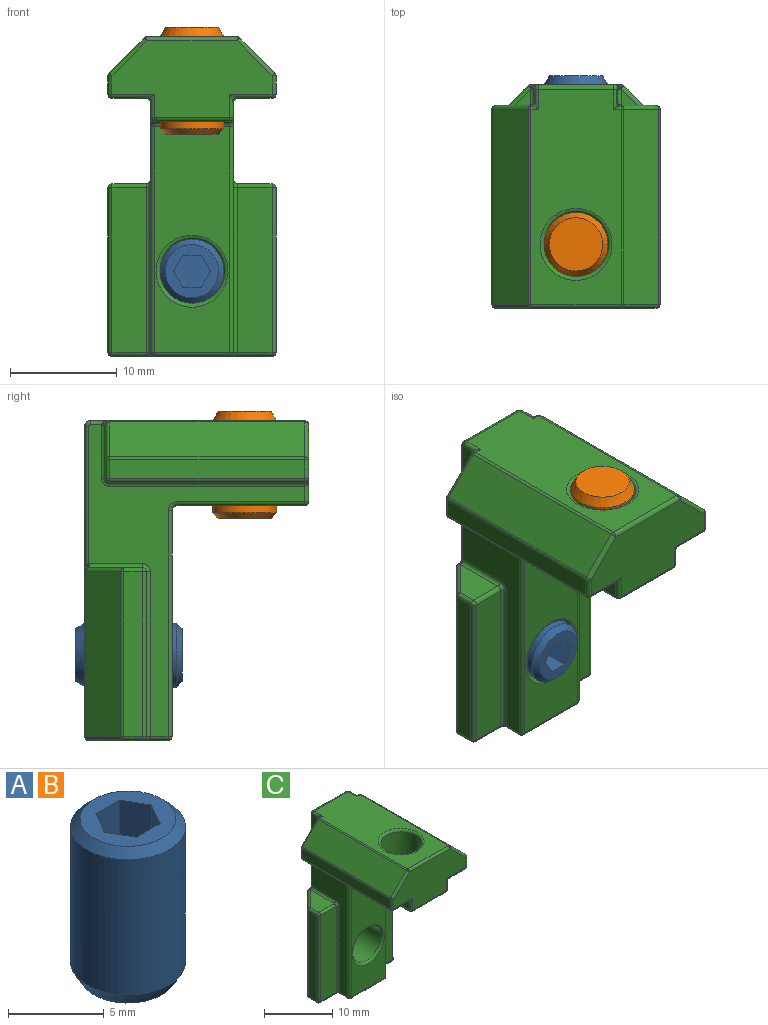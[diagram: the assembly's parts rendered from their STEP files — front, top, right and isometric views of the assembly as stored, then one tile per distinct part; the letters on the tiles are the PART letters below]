
ASSEMBLY  parts=3 mates=2
PART A: 12 faces, bbox 6x6x10 mm
  f0: cone r=3mm half-angle=45deg, axis (0,0,-1), area 12.2mm2, adj f2,f3
  f1: cone r=2.5mm half-angle=30deg, axis (0,0,1), area 17.3mm2, adj f2,f4
  f2: cylinder r=3mm len=8.63mm, axis (0,0,-1), area 162.7mm2, adj f0,f1
  f3: plane 5x5mm, normal (0,0,1), area 11.8mm2, adj f0,f5,f6,f7,f8,f9,f10
  f4: plane 5x5mm, normal (0,0,-1), area 19.6mm2, adj f1
  f5: plane 3x1.73mm, normal (0,-1,0), area 5.2mm2, adj f3,f6,f10,f11
  f6: plane 3x1.5mm, normal (-0.87,-0.5,0), area 5.2mm2, adj f3,f5,f7,f11
  f7: plane 3x1.5mm, normal (-0.87,0.5,0), area 5.2mm2, adj f3,f6,f8,f11
  f8: plane 3x1.73mm, normal (0,1,0), area 5.2mm2, adj f3,f7,f9,f11
  f9: plane 3x1.5mm, normal (0.87,0.5,0), area 5.2mm2, adj f3,f8,f10,f11
  f10: plane 3x1.5mm, normal (0.87,-0.5,0), area 5.2mm2, adj f3,f5,f9,f11
  f11: plane 3.46x3mm, normal (0,0,1), area 7.8mm2, adj f5,f6,f7,f8,f9,f10
PART B: same geometry as A
PART C: 152 faces, bbox 15.8x21x30 mm
  f0: torus R=3.38mm, axis (0,1,0), area 11.8mm2, adj f5,f10
  f1: torus R=3.38mm, axis (0,-1,0), area 11.8mm2, adj f5,f6
  f2: torus R=3.38mm, axis (0,0,1), area 11.8mm2, adj f4,f9
  f3: torus R=3.38mm, axis (0,0,-1), area 11.8mm2, adj f4,f7
  f4: cylinder r=3mm len=7.19mm, axis (0,0,-1), area 135.5mm2, adj f2,f3
  f5: cylinder r=3mm len=7.44mm, axis (0,-1,0), area 140.3mm2, adj f0,f1
  f6: plane 29.11x8.45mm, normal (0,1,0), area 190.7mm2, adj f1,f31,f32,f33,f34,f37,f40,f41
  f7: plane 20.12x8.45mm, normal (0,0,1), area 131.4mm2, adj f3,f31,f45,f50,f51,f60,f67,f74
  f8: plane 15.01x7.19mm, normal (0,-1,0), area 79.9mm2, adj f75,f82,f91,f99,f104,f109,f112,f113
  f9: plane 11.91x7.04mm, normal (0,0,-1), area 47.9mm2, adj f2,f30,f114,f115,f119
  f10: plane 21.16x7.04mm, normal (0,-1,0), area 113mm2, adj f0,f30,f95,f106,f107
  f11: plane 15.01x7.44mm, normal (0,0,-1), area 81.7mm2, adj f41,f55,f56,f70,f71,f86,f87,f94
  f12: plane 29.24x20.24mm, normal (1,0,0), area 105.8mm2, adj f34,f38,f45,f94,f106,f110,f113,f114
  f13: plane 29.24x20.25mm, normal (-1,0,0), area 105.8mm2, adj f37,f44,f50,f96,f107,f111,f115,f116
  f14: plane 15.44x3.28mm, normal (-0.71,0.71,0), area 71.7mm2, adj f42,f43,f56,f57
  f15: plane 15.44x1.75mm, normal (-1,0,0), area 27mm2, adj f57,f58,f71,f72
  f16: plane 4.97x3.23mm, normal (0,0,1), area 10.8mm2, adj f43,f58,f59,f141
  f17: plane 15.44x3.23mm, normal (0,-1,0), area 49.8mm2, adj f59,f72,f87,f142
  f18: plane 15.44x3.23mm, normal (0,-1,0), area 49.8mm2, adj f52,f69,f86,f149
  f19: plane 4.97x3.23mm, normal (0,0,1), area 10.8mm2, adj f39,f52,f53,f150
  f20: plane 15.44x1.75mm, normal (1,0,0), area 27mm2, adj f53,f54,f69,f70
  f21: plane 15.44x3.28mm, normal (0.71,0.71,0), area 71.7mm2, adj f39,f40,f54,f55
  f22: plane 18.29x1.75mm, normal (-1,0,0), area 32mm2, adj f89,f90,f103,f104
  f23: plane 18.29x3.28mm, normal (-0.71,0,0.71), area 84.9mm2, adj f73,f74,f90,f91
  f24: plane 4.97x3.23mm, normal (0,1,0), area 10.8mm2, adj f73,f88,f89,f123
  f25: plane 18.29x3.23mm, normal (0,0,-1), area 59mm2, adj f88,f103,f112,f121
  f26: plane 18.29x3.23mm, normal (0,0,-1), area 59mm2, adj f85,f100,f109,f129
  f27: plane 4.97x3.23mm, normal (0,1,0), area 10.8mm2, adj f68,f84,f85,f131
  f28: plane 18.29x3.28mm, normal (0.71,0,0.71), area 84.9mm2, adj f67,f68,f82,f83
  f29: plane 18.29x1.75mm, normal (1,0,0), area 32mm2, adj f83,f84,f99,f100
  f30: cylinder r=0.51mm len=7.04mm, axis (1,0,0), area 5.6mm2, adj f9,f10,f110,f111
  f31: cylinder r=0.51mm len=7.04mm, axis (-1,0,0), area 5.6mm2, adj f6,f7,f38,f44
  f32: cylinder r=0.38mm len=0.71mm, axis (1,0,0), area 0.2mm2, adj f6,f35,f144
  f33: cylinder r=0.38mm len=0.71mm, axis (1,0,0), area 0.2mm2, adj f6,f36,f136
  f34: cylinder r=0.38mm len=13.67mm, axis (0,0,1), area 7.9mm2, adj f6,f12,f38,f144,f145,f146
  f35: sphere r=0.38mm, area 0.1mm2, adj f32,f39,f40,f145
  f36: sphere r=0.38mm, area 0.1mm2, adj f33,f42,f43,f137
  f37: cylinder r=0.38mm len=13.67mm, axis (0,0,-1), area 7.9mm2, adj f6,f13,f44,f136,f137,f138
  f38: torus R=0.13mm, axis (-1,0,0), area 0.3mm2, adj f12,f31,f34,f45
  f39: cylinder r=0.38mm len=3.55mm, axis (-0.71,0.71,0), area 2.8mm2, adj f19,f21,f35,f46,f146,f148
  f40: cylinder r=0.38mm len=15.44mm, axis (0,0,1), area 4.6mm2, adj f6,f21,f35,f47
  f41: cylinder r=0.38mm len=8.45mm, axis (-1,0,0), area 5.1mm2, adj f6,f11,f47,f48
  f42: cylinder r=0.38mm len=15.44mm, axis (0,0,1), area 4.6mm2, adj f6,f14,f36,f48
  f43: cylinder r=0.38mm len=3.55mm, axis (-0.71,-0.71,0), area 2.8mm2, adj f14,f16,f36,f49,f138,f139
  f44: torus R=0.13mm, axis (-1,0,0), area 0.3mm2, adj f13,f31,f37,f50
  f45: cylinder r=0.38mm len=1.83mm, axis (0,-1,0), area 0.8mm2, adj f7,f12,f38,f133,f134,f135
  f46: sphere r=0.38mm, area 0.1mm2, adj f39,f53,f54
  f47: sphere r=0.38mm, area 0.1mm2, adj f40,f41,f55
  f48: sphere r=0.38mm, area 0.1mm2, adj f41,f42,f56
  f49: sphere r=0.38mm, area 0.1mm2, adj f43,f57,f58
  f50: cylinder r=0.38mm len=1.83mm, axis (0,1,0), area 0.8mm2, adj f7,f13,f44,f125,f126,f127
  f51: cylinder r=0.38mm len=0.71mm, axis (1,0,0), area 0.2mm2, adj f7,f61,f134
  f52: cylinder r=0.38mm len=3.23mm, axis (1,0,0), area 1.9mm2, adj f18,f19,f62,f151
  f53: cylinder r=0.38mm len=1.75mm, axis (0,1,0), area 1mm2, adj f19,f20,f46,f62
  f54: cylinder r=0.38mm len=15.44mm, axis (0,0,-1), area 4.6mm2, adj f20,f21,f46,f63
  f55: cylinder r=0.38mm len=3.55mm, axis (-0.71,0.71,0), area 2.8mm2, adj f11,f21,f47,f63
  f56: cylinder r=0.38mm len=3.55mm, axis (-0.71,-0.71,0), area 2.8mm2, adj f11,f14,f48,f64
  f57: cylinder r=0.38mm len=15.44mm, axis (0,0,-1), area 4.6mm2, adj f14,f15,f49,f64
  f58: cylinder r=0.38mm len=1.75mm, axis (0,-1,0), area 1mm2, adj f15,f16,f49,f65
  f59: cylinder r=0.38mm len=3.23mm, axis (1,0,0), area 1.9mm2, adj f16,f17,f65,f143
  f60: cylinder r=0.38mm len=0.71mm, axis (1,0,0), area 0.2mm2, adj f7,f66,f127
  f61: sphere r=0.38mm, area 0.1mm2, adj f51,f67,f68,f135
  f62: sphere r=0.38mm, area 0.2mm2, adj f52,f53,f69
  f63: sphere r=0.38mm, area 0.1mm2, adj f54,f55,f70
  f64: sphere r=0.38mm, area 0.1mm2, adj f56,f57,f71
  f65: sphere r=0.38mm, area 0.2mm2, adj f58,f59,f72
  f66: sphere r=0.38mm, area 0.1mm2, adj f60,f73,f74,f126
  f67: cylinder r=0.38mm len=18.29mm, axis (0,1,0), area 5.5mm2, adj f7,f28,f61,f76
  f68: cylinder r=0.38mm len=3.55mm, axis (-0.71,0,0.71), area 2.8mm2, adj f27,f28,f61,f77,f132,f133
  f69: cylinder r=0.38mm len=15.44mm, axis (0,0,-1), area 9.2mm2, adj f18,f20,f62,f78
  f70: cylinder r=0.38mm len=1.75mm, axis (0,1,0), area 1mm2, adj f11,f20,f63,f78
  f71: cylinder r=0.38mm len=1.75mm, axis (0,-1,0), area 1mm2, adj f11,f15,f64,f79
  f72: cylinder r=0.38mm len=15.44mm, axis (0,0,-1), area 9.2mm2, adj f15,f17,f65,f79
  f73: cylinder r=0.38mm len=3.55mm, axis (-0.71,0,-0.71), area 2.8mm2, adj f23,f24,f66,f80,f124,f125
  f74: cylinder r=0.38mm len=18.29mm, axis (0,1,0), area 5.5mm2, adj f7,f23,f66,f81
  f75: cylinder r=0.38mm len=8.45mm, axis (-1,0,0), area 5.1mm2, adj f7,f8,f76,f81
  f76: sphere r=0.38mm, area 0.1mm2, adj f67,f75,f82
  f77: sphere r=0.38mm, area 0.1mm2, adj f68,f83,f84
  f78: sphere r=0.38mm, area 0.1mm2, adj f69,f70,f86
  f79: sphere r=0.38mm, area 0.1mm2, adj f71,f72,f87
  f80: sphere r=0.38mm, area 0.1mm2, adj f73,f89,f90
  f81: sphere r=0.38mm, area 0.1mm2, adj f74,f75,f91
  f82: cylinder r=0.38mm len=3.55mm, axis (0.71,0,-0.71), area 2.8mm2, adj f8,f28,f76,f92
  f83: cylinder r=0.38mm len=18.29mm, axis (0,-1,0), area 5.5mm2, adj f28,f29,f77,f92
  f84: cylinder r=0.38mm len=1.75mm, axis (0,0,1), area 1mm2, adj f27,f29,f77,f93
  f85: cylinder r=0.38mm len=3.23mm, axis (1,0,0), area 1.9mm2, adj f26,f27,f93,f130
  f86: cylinder r=0.38mm len=3.99mm, axis (1,0,0), area 2.2mm2, adj f11,f18,f78,f147
  f87: cylinder r=0.38mm len=3.99mm, axis (1,0,0), area 2.2mm2, adj f11,f17,f79,f140
  f88: cylinder r=0.38mm len=3.23mm, axis (1,0,0), area 1.9mm2, adj f24,f25,f97,f122
  f89: cylinder r=0.38mm len=1.75mm, axis (0,0,-1), area 1mm2, adj f22,f24,f80,f97
  f90: cylinder r=0.38mm len=18.29mm, axis (0,-1,0), area 5.5mm2, adj f22,f23,f80,f98
  f91: cylinder r=0.38mm len=3.55mm, axis (0.71,0,0.71), area 2.8mm2, adj f8,f23,f81,f98
  f92: sphere r=0.38mm, area 0.1mm2, adj f82,f83,f99
  f93: sphere r=0.38mm, area 0.1mm2, adj f84,f85,f100
  f94: cylinder r=0.38mm len=2.41mm, axis (0,1,0), area 1.2mm2, adj f11,f12,f101,f147
  f95: cylinder r=0.38mm len=7.04mm, axis (-1,0,0), area 4.2mm2, adj f10,f11,f101,f102
  f96: cylinder r=0.38mm len=2.41mm, axis (0,-1,0), area 1.2mm2, adj f11,f13,f102,f140
  f97: sphere r=0.38mm, area 0.3mm2, adj f88,f89,f103
  f98: sphere r=0.38mm, area 0.1mm2, adj f90,f91,f104
  f99: cylinder r=0.38mm len=1.75mm, axis (0,0,-1), area 1mm2, adj f8,f29,f92,f105
  f100: cylinder r=0.38mm len=18.29mm, axis (0,-1,0), area 10.9mm2, adj f26,f29,f93,f105
  f101: sphere r=0.38mm, area 0.1mm2, adj f94,f95,f106
  f102: sphere r=0.38mm, area 0.3mm2, adj f95,f96,f107
  f103: cylinder r=0.38mm len=18.29mm, axis (0,-1,0), area 10.9mm2, adj f22,f25,f97,f108
  f104: cylinder r=0.38mm len=1.75mm, axis (0,0,1), area 1mm2, adj f8,f22,f98,f108
  f105: sphere r=0.38mm, area 0.1mm2, adj f99,f100,f109
  f106: cylinder r=0.38mm len=21.16mm, axis (0,0,-1), area 12.7mm2, adj f10,f12,f101,f110
  f107: cylinder r=0.38mm len=21.16mm, axis (0,0,1), area 12.7mm2, adj f10,f13,f102,f111
  f108: sphere r=0.38mm, area 0.3mm2, adj f103,f104,f112
  f109: cylinder r=0.38mm len=3.99mm, axis (-1,0,0), area 2.2mm2, adj f8,f26,f105,f128
  f110: torus R=0.89mm, axis (-1,0,0), area 0.6mm2, adj f12,f30,f106,f114
  f111: torus R=0.89mm, axis (-1,0,0), area 0.6mm2, adj f13,f30,f107,f115
  f112: cylinder r=0.38mm len=3.99mm, axis (-1,0,0), area 2.2mm2, adj f8,f25,f108,f120
  f113: cylinder r=0.38mm len=2.16mm, axis (0,0,-1), area 1.1mm2, adj f8,f12,f117,f128
  f114: cylinder r=0.38mm len=11.91mm, axis (0,1,0), area 7.1mm2, adj f9,f12,f110,f117
  f115: cylinder r=0.38mm len=11.91mm, axis (0,-1,0), area 7.1mm2, adj f9,f13,f111,f118
  f116: cylinder r=0.38mm len=2.16mm, axis (0,0,1), area 1.1mm2, adj f8,f13,f118,f120
  f117: sphere r=0.38mm, area 0.1mm2, adj f113,f114,f119
  f118: sphere r=0.38mm, area 0.3mm2, adj f115,f116,f119
  f119: cylinder r=0.38mm len=7.04mm, axis (-1,0,0), area 4.2mm2, adj f8,f9,f117,f118
  f120: bspline ~0.76x0.76mm, area 0.2mm2, adj f112,f116,f121
  f121: cylinder r=0.38mm len=18.29mm, axis (0,1,0), area 10.9mm2, adj f13,f25,f120,f122
  f122: torus R=0.76mm, axis (-1,0,0), area 0.5mm2, adj f13,f88,f121,f123
  f123: cylinder r=0.38mm len=4.97mm, axis (0,0,1), area 3mm2, adj f13,f24,f122,f124
  f124: cylinder r=0.38mm len=0.38mm, axis (-0.02,-0.04,1), area 0mm2, adj f13,f73,f123,f125
  f125: bspline ~0.38x0.37mm, area 0mm2, adj f50,f73,f124,f126
  f126: bspline ~0.41x0.38mm, area 0.1mm2, adj f50,f66,f125,f127
  f127: bspline ~0.71x0.71mm, area 0.1mm2, adj f50,f60,f126
  f128: bspline ~0.76x0.76mm, area 0.2mm2, adj f109,f113,f129
  f129: cylinder r=0.38mm len=18.29mm, axis (0,-1,0), area 10.9mm2, adj f12,f26,f128,f130
  f130: torus R=0.76mm, axis (-1,0,0), area 0.5mm2, adj f12,f85,f129,f131
  f131: cylinder r=0.38mm len=4.97mm, axis (0,0,-1), area 3mm2, adj f12,f27,f130,f132
  f132: cylinder r=0.38mm len=0.38mm, axis (0,-0.01,1), area 0mm2, adj f12,f68,f131,f133
  f133: bspline ~0.38x0.37mm, area 0mm2, adj f45,f68,f132,f135
  f134: bspline ~0.71x0.71mm, area 0.1mm2, adj f45,f51,f135
  f135: bspline ~0.41x0.38mm, area 0.1mm2, adj f45,f61,f133,f134
  f136: bspline ~0.71x0.71mm, area 0.1mm2, adj f33,f37,f137
  f137: bspline ~0.41x0.38mm, area 0.1mm2, adj f36,f37,f136,f138
  f138: bspline ~0.38x0.37mm, area 0mm2, adj f37,f43,f137,f139
  f139: cylinder r=0.38mm len=0.38mm, axis (-0.02,-1,0), area 0mm2, adj f13,f43,f138,f141
  f140: bspline ~0.76x0.76mm, area 0.2mm2, adj f87,f96,f142
  f141: cylinder r=0.38mm len=4.97mm, axis (0,-1,0), area 3mm2, adj f13,f16,f139,f143
  f142: cylinder r=0.38mm len=15.44mm, axis (0,0,-1), area 9.2mm2, adj f13,f17,f140,f143
  f143: torus R=0.76mm, axis (-1,0,0), area 0.5mm2, adj f13,f59,f141,f142
  f144: bspline ~0.71x0.71mm, area 0.1mm2, adj f32,f34,f145
  f145: bspline ~0.41x0.38mm, area 0.1mm2, adj f34,f35,f144,f146
  f146: bspline ~0.38x0.37mm, area 0mm2, adj f34,f39,f145,f148
  f147: bspline ~0.76x0.76mm, area 0.2mm2, adj f86,f94,f149
  f148: cylinder r=0.38mm len=0.38mm, axis (0,-1,0.02), area 0mm2, adj f12,f39,f146,f150
  f149: cylinder r=0.38mm len=15.44mm, axis (0,0,1), area 9.2mm2, adj f12,f18,f147,f151
  f150: cylinder r=0.38mm len=4.97mm, axis (0,1,0), area 3mm2, adj f12,f19,f148,f151
  f151: torus R=0.76mm, axis (-1,0,0), area 0.5mm2, adj f12,f52,f149,f150
PLACE A rot(axis=(1,0,0),90deg) t=(3.1,17.66,3.95)mm
PLACE B rot(axis=(0,1,0),180deg) t=(3.1,1.79,26.81)mm
PLACE C t=(3.1,16.8,25.94)mm
MATE fastened B.f0 <-> C.f2  axis (0,0,-1) through (3.1,1.79,25.94)mm
MATE fastened A.f0 <-> C.f1  axis (0,-1,0) through (3.1,16.8,3.95)mm
